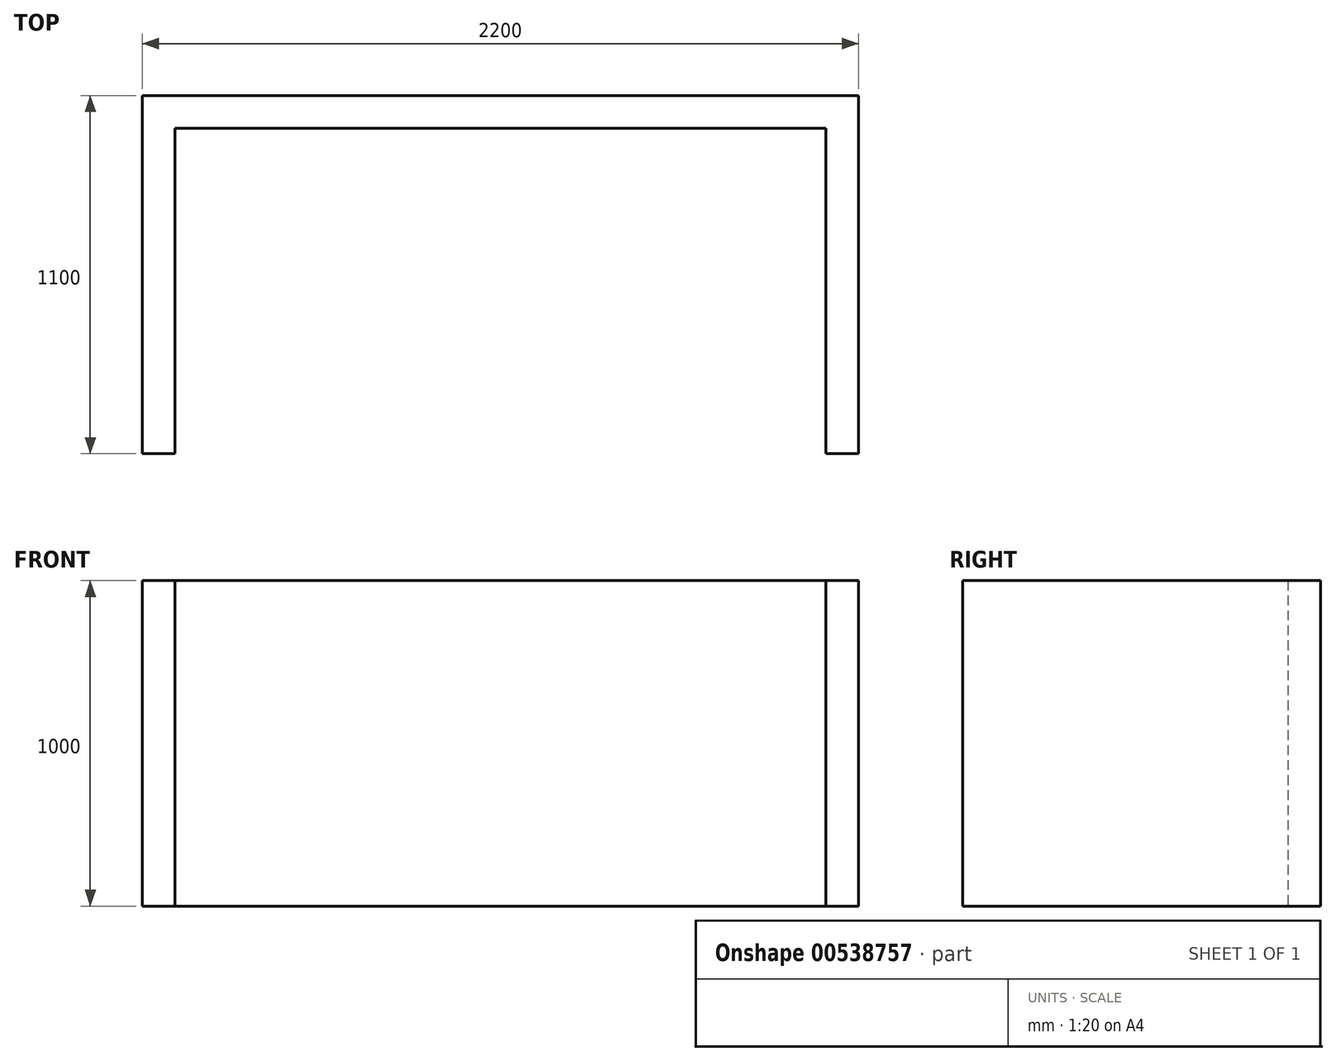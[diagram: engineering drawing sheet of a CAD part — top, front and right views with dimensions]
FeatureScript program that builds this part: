
annotation { "Feature Type Name" : "Feature", "Feature Type Description" : "" }
export const myFeature = defineFeature(function(context is Context, id is Id, definition is map)
    precondition{}
    {
        {
            var Q0;
            Q0=qCreatedBy(makeId("Top.planeOp"),FACE);
            var sketch = newSketch(context, id + "F0", { "sketchPlane" : qUnion([Q0])});
            skLineSegment(sketch, "E0", {"start": v(-1510.67, -244.21) * mm, "end": v(-1510.67, 755.79) * mm});
            skLineSegment(sketch, "E1", {"start": v(-1510.67, 755.79) * mm, "end": v(489.33, 755.79) * mm});
            skLineSegment(sketch, "E2", {"start": v(489.33, 755.79) * mm, "end": v(489.33, -244.21) * mm});
            skLineSegment(sketch, "E3", {"start": v(489.33, -244.21) * mm, "end": v(589.33, -244.21) * mm});
            skLineSegment(sketch, "E4", {"start": v(589.33, -244.21) * mm, "end": v(589.33, 855.79) * mm});
            skLineSegment(sketch, "E5", {"start": v(589.33, 855.79) * mm, "end": v(-1610.67, 855.79) * mm});
            skLineSegment(sketch, "E6", {"start": v(-1610.67, 855.79) * mm, "end": v(-1610.67, -244.21) * mm});
            skLineSegment(sketch, "E7", {"start": v(-1610.67, -244.21) * mm, "end": v(-1510.67, -244.21) * mm});
            skSolve(sketch);
        }
        {
            var Q0;
            Q0=makeQuery(id+"F0.imprint","IMPRINT",FACE,{"disambiguationData":[TD([[makeQuery(id+"F0.imprint","IMPRINT",EDGE,{"derivedFrom":sQuery(id+"F0.wireOp",EDGE,"E0")}),1.0]])]});
            extrude(context, id + "F1", {"entities" : qUnion([Q0]), "depth" : 1000 * mm, "offsetDistance" : 25 * mm});
        }
    });
